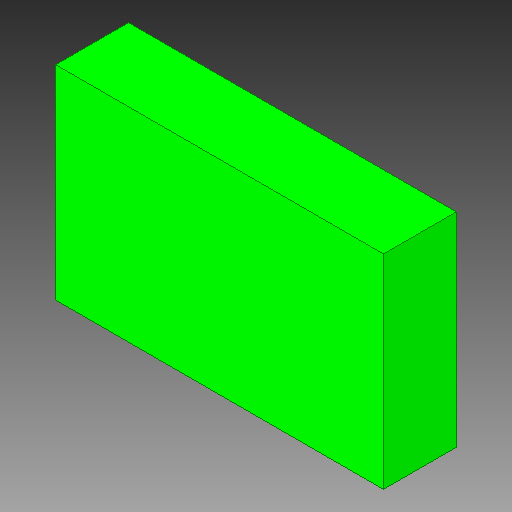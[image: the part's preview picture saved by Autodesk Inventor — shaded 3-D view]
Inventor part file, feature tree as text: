
AUTODESK INVENTOR PART (.ipt)
format: ipt  version: 2018 (Build 220112000, 112)  size: 80,896 bytes
history: native  units: in
note: dims shown in document units (in); Inventor stores cm internally (conversion verified against a paired STEP export)
features: other x1, extrude x1
ambient origin geometry x8: Origin, YZ Plane, XZ Plane, XY Plane, X Axis, Y Axis, Z Axis, Center Point
bodies: Solid1 (feature_tree)
feature tree (2):
  other  "MURATA-FILTER_CSTCR, CSTCR4M00G15L99_93"
  extrude  "Extrusion1"  Depth=0.0394in TaperAngle=0.0deg
